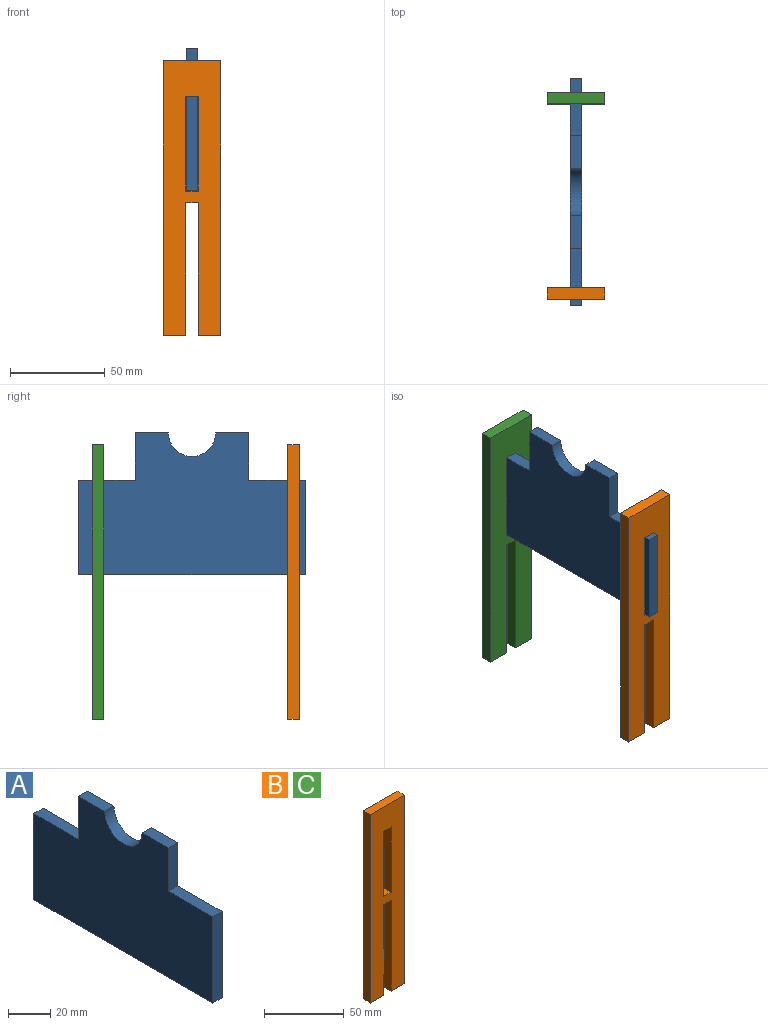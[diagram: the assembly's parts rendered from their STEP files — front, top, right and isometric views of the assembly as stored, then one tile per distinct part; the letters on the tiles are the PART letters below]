
ASSEMBLY  parts=3 mates=2
PART A: 12 faces, bbox 6.2x120x75 mm
  f0: cylinder r=12.5mm len=25mm, axis (-1,0,0), area 243.5mm2, adj f1,f9,f10,f11
  f1: plane 17.5x6.2mm, normal (0,0,1), area 108.5mm2, adj f0,f2,f10,f11
  f2: plane 25x6.2mm, normal (0,-1,0), area 155mm2, adj f1,f3,f10,f11
  f3: plane 30x6.2mm, normal (0,0,1), area 186mm2, adj f2,f4,f10,f11
  f4: plane 50x6.2mm, normal (0,-1,0), area 310mm2, adj f3,f5,f10,f11
  f5: plane 120x6.2mm, normal (0,0,-1), area 744mm2, adj f4,f6,f10,f11
  f6: plane 50x6.2mm, normal (0,1,0), area 310mm2, adj f5,f7,f10,f11
  f7: plane 30x6.2mm, normal (0,0,1), area 186mm2, adj f6,f8,f10,f11
  f8: plane 25x6.2mm, normal (0,1,0), area 155mm2, adj f7,f9,f10,f11
  f9: plane 17.5x6.2mm, normal (0,0,1), area 108.5mm2, adj f0,f8,f10,f11
  f10: plane 120x75mm, normal (1,0,0), area 7254.6mm2, adj f0,f1,f2,f3,f4,f5,f6,f7
  f11: plane 120x75mm, normal (-1,0,0), area 7254.6mm2, adj f0,f1,f2,f3,f4,f5,f6,f7
PART B: 14 faces, bbox 30.4x6.2x145 mm
  f0: plane 6.4x6.2mm, normal (0,0,-1), area 39.7mm2, adj f1,f11,f12,f13
  f1: plane 70x6.2mm, normal (-1,0,0), area 434mm2, adj f0,f2,f12,f13
  f2: plane 12x6.2mm, normal (0,0,-1), area 74.4mm2, adj f1,f3,f12,f13
  f3: plane 145x6.2mm, normal (1,0,0), area 899mm2, adj f2,f4,f12,f13
  f4: plane 30.4x6.2mm, normal (0,0,1), area 188.5mm2, adj f3,f5,f12,f13
  f5: plane 145x6.2mm, normal (-1,0,0), area 899mm2, adj f4,f6,f12,f13
  f6: plane 12x6.2mm, normal (0,0,-1), area 74.4mm2, adj f5,f11,f12,f13
  f7: plane 6.4x6.2mm, normal (0,0,1), area 39.7mm2, adj f8,f10,f12,f13
  f8: plane 50.2x6.2mm, normal (1,0,0), area 311.2mm2, adj f7,f9,f12,f13
  f9: plane 6.4x6.2mm, normal (0,0,-1), area 39.7mm2, adj f8,f10,f12,f13
  f10: plane 50.2x6.2mm, normal (-1,0,0), area 311.2mm2, adj f7,f9,f12,f13
  f11: plane 70x6.2mm, normal (1,0,0), area 434mm2, adj f0,f6,f12,f13
  f12: plane 145x30.4mm, normal (0,-1,0), area 3638.7mm2, adj f0,f1,f2,f3,f4,f5,f6,f7
  f13: plane 145x30.4mm, normal (0,1,0), area 3638.7mm2, adj f0,f1,f2,f3,f4,f5,f6,f7
PART C: same geometry as B
PLACE A t=(-2.71,-49.53,59.13)mm
PLACE B t=(0.39,-100.13,-22.27)mm
PLACE C t=(0.39,3.21,-22.27)mm fixed
MATE slider A.f4 <-> B.f12  axis (0,-1,0) through (0.39,-109.53,34.13)mm
MATE slider A.f6 <-> C.f13  axis (0,1,0) through (0.39,10.47,34.13)mm
